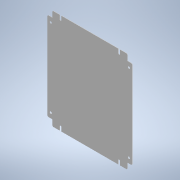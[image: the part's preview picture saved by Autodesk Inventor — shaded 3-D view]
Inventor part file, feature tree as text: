
AUTODESK INVENTOR PART (.ipt)
format: ipt  version: 2021 (Build 250183000, 183)  size: 150,528 bytes
history: native  units: mm
features: other x7, extrude x1, sketch x1
ambient origin geometry x8: Origin, YZ Plane, XZ Plane, XY Plane, X Axis, Y Axis, Z Axis, Center Point
bodies: Solid1 (feature_tree)
feature tree (9):
  extrude  "Extrusion1"  TaperAngle=0.0deg  [1 undecoded]
  other  "to_frame_XY"
  other  "to_frame_YZ"
  other  "to_frame_ZX"
  other  "to_frame_X"
  other  "to_frame_Y"
  other  "to_frame_Z"
  other  "to_frame_Center"
  sketch  "Sketch_1"  dims[d0=1.5mm d1=0.0mm d2=0.0mm]
note: 1 required parameter value undecoded (feature->parameter linkage not recoverable at this tier; creation-order binding heuristic only, values carry confidence <= 0.55)
